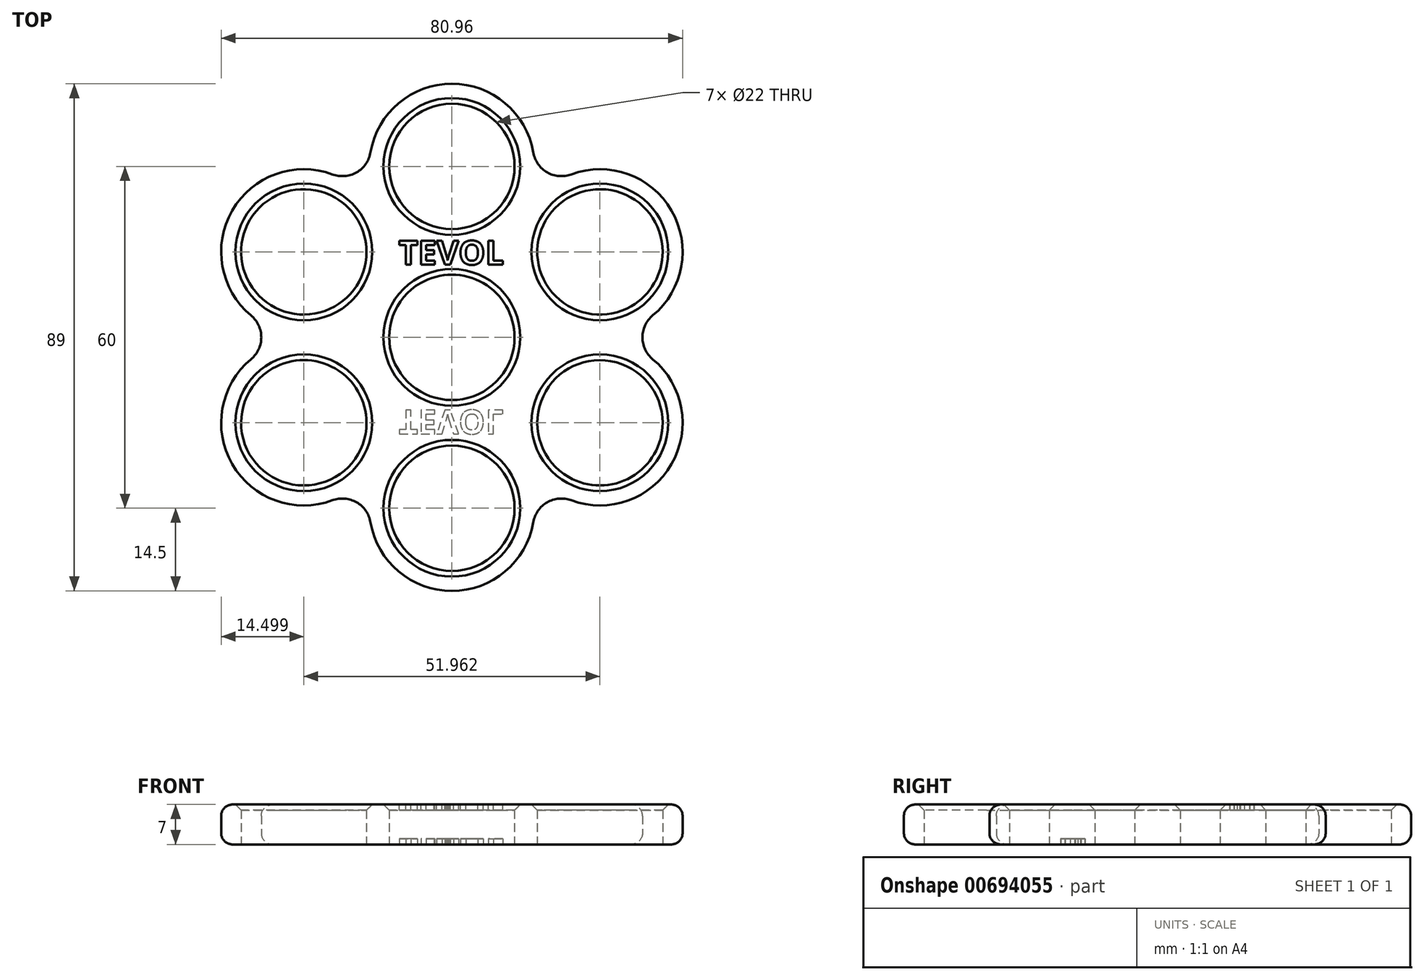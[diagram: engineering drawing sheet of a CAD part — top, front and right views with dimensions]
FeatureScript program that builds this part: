
annotation { "Feature Type Name" : "Feature", "Feature Type Description" : "" }
export const myFeature = defineFeature(function(context is Context, id is Id, definition is map)
    precondition{}
    {
        {
            var Q0;
            Q0=qCreatedBy(makeId("Top.planeOp"),FACE);
            var sketch = newSketch(context, id + "F0", { "sketchPlane" : qUnion([Q0])});
            skCircle(sketch, "E0", {"center": v(0, 0) * mm, "radius": 14.5 * mm});
            skCircle(sketch, "E1", {"center": v(0, -30) * mm, "radius": 14.5 * mm});
            skLineSegment(sketch, "E2", {"start": v(14.5, 0) * mm, "end": v(14.5, -30) * mm});
            skLineSegment(sketch, "E3", {"start": v(-14.5, 0) * mm, "end": v(-14.5, -30) * mm});
            skSolve(sketch);
        }
        {
            var Q0;
            Q0=qSketchRegion(id+"F0",true);
            var Q1;
            {var subQ0=sQuery(id+"F0.wireOp",EDGE,"E1");var subQ1=sQuery(id+"F0.wireOp",EDGE,"E0");var subQ2=makeQuery(id+"F0.imprint","INTERSECT",VERTEX,{"disambiguationData":[OD(0.0)],"derivedFrom":[subQ1,subQ0]});Q1=makeQuery(id+"F0.imprint","IMPRINT",FACE,{"disambiguationData":[TD([[makeQuery(id+"F0.imprint","IMPRINT",EDGE,{"disambiguationData":[TD([[subQ2,-1.0]])],"derivedFrom":subQ1}),1.0]])]});}
            extrude(context, id + "F1", {"entities" : qUnion([Q0, Q1]), "depth" : 7 * mm, "offsetDistance" : 25 * mm});
        }
        {
            var Q0;
            Q0=makeQuery(id+"F1.opExtrude","CAP_FACE",FACE,{"disambiguationData":[OSD([sQuery(id+"F0.wireOp",EDGE,"E0"),sQuery(id+"F0.wireOp",EDGE,"E1"),sQuery(id+"F0.wireOp",EDGE,"E2"),sQuery(id+"F0.wireOp",EDGE,"E3")])],"isStart":false});
            var sketch = newSketch(context, id + "F2", { "sketchPlane" : qUnion([Q0])});
            skCircle(sketch, "E4", {"center": v(0, 0) * mm, "radius": 11 * mm});
            skCircle(sketch, "E5", {"center": v(0, -30) * mm, "radius": 11 * mm});
            skLineSegment(sketch, "E6", {"start": v(0, 0) * mm, "end": v(0, -30) * mm});
            skSolve(sketch);
        }
        {
            var Q0;
            Q0=qSketchRegion(id+"F2",true);
            extrude(context, id + "F3", {"entities" : qUnion([Q0]), "operationType" : NewBodyOperationType.REMOVE, "endBound" : BoundingType.THROUGH_ALL, "oppositeDirection" : true, "depth" : 25 * mm, "offsetDistance" : 25 * mm});
        }
        {
            var Q0;
            Q0=qCreatedBy(makeId("Front.planeOp"),FACE);
            var sketch = newSketch(context, id + "F4", { "sketchPlane" : qUnion([Q0])});
            skLineSegment(sketch, "E7", {"start": v(0, 0) * mm, "end": v(0, 26.48) * mm});
            skSolve(sketch);
        }
        {
            var Q0;
            Q0=makeQuery(id+"F1.opExtrude","SWEPT_BODY",BODY,{"disambiguationData":[OSD([sQuery(id+"F0.wireOp",EDGE,"E0"),sQuery(id+"F0.wireOp",EDGE,"E1"),sQuery(id+"F0.wireOp",EDGE,"E2"),sQuery(id+"F0.wireOp",EDGE,"E3")])]});
            var Q1;
            Q1=sQuery(id+"F4.wireOp",EDGE,"E7");
            circularPattern(context, id + "F5", {"entities" : qUnion([Q0]), "axis" : qUnion([Q1]), "angle" : 360 * degree, "instanceCount" : 6, "equalSpace" : true});
        }
        {
            var Q0;
            Q0=makeQuery(id+"F5.opPattern","COPY",BODY,{"derivedFrom":makeQuery(id+"F1.opExtrude","SWEPT_BODY",BODY,{"disambiguationData":[OSD([sQuery(id+"F0.wireOp",EDGE,"E0"),sQuery(id+"F0.wireOp",EDGE,"E1"),sQuery(id+"F0.wireOp",EDGE,"E2"),sQuery(id+"F0.wireOp",EDGE,"E3")])]}),"instanceName":"4"});
            var Q1;
            Q1=makeQuery(id+"F5.opPattern","COPY",BODY,{"derivedFrom":makeQuery(id+"F1.opExtrude","SWEPT_BODY",BODY,{"disambiguationData":[OSD([sQuery(id+"F0.wireOp",EDGE,"E0"),sQuery(id+"F0.wireOp",EDGE,"E1"),sQuery(id+"F0.wireOp",EDGE,"E2"),sQuery(id+"F0.wireOp",EDGE,"E3")])]}),"instanceName":"3"});
            var Q2;
            Q2=makeQuery(id+"F5.opPattern","COPY",BODY,{"derivedFrom":makeQuery(id+"F1.opExtrude","SWEPT_BODY",BODY,{"disambiguationData":[OSD([sQuery(id+"F0.wireOp",EDGE,"E0"),sQuery(id+"F0.wireOp",EDGE,"E1"),sQuery(id+"F0.wireOp",EDGE,"E2"),sQuery(id+"F0.wireOp",EDGE,"E3")])]}),"instanceName":"2"});
            var Q3;
            Q3=makeQuery(id+"F5.opPattern","COPY",BODY,{"derivedFrom":makeQuery(id+"F1.opExtrude","SWEPT_BODY",BODY,{"disambiguationData":[OSD([sQuery(id+"F0.wireOp",EDGE,"E0"),sQuery(id+"F0.wireOp",EDGE,"E1"),sQuery(id+"F0.wireOp",EDGE,"E2"),sQuery(id+"F0.wireOp",EDGE,"E3")])]}),"instanceName":"1"});
            var Q4;
            Q4=makeQuery(id+"F1.opExtrude","SWEPT_BODY",BODY,{"disambiguationData":[OSD([sQuery(id+"F0.wireOp",EDGE,"E0"),sQuery(id+"F0.wireOp",EDGE,"E1"),sQuery(id+"F0.wireOp",EDGE,"E2"),sQuery(id+"F0.wireOp",EDGE,"E3")])]});
            var Q5;
            Q5=makeQuery(id+"F5.opPattern","COPY",BODY,{"derivedFrom":makeQuery(id+"F1.opExtrude","SWEPT_BODY",BODY,{"disambiguationData":[OSD([sQuery(id+"F0.wireOp",EDGE,"E0"),sQuery(id+"F0.wireOp",EDGE,"E1"),sQuery(id+"F0.wireOp",EDGE,"E2"),sQuery(id+"F0.wireOp",EDGE,"E3")])]}),"instanceName":"5"});
            booleanBodies(context, id + "F6", {"operationType" : BooleanOperationType.UNION, "tools" : qUnion([Q0, Q1, Q2, Q3, Q4, Q5])});
        }
        {
            var Q0;
            Q0=makeQuery(id+"F6.opBoolean","INTERSECT",EDGE,{"derivedFrom":[makeQuery(id+"F5.opPattern","COPY",FACE,{"derivedFrom":makeQuery(id+"F1.opExtrude","SWEPT_FACE",FACE,{"disambiguationData":[OSD([sQuery(id+"F0.wireOp",EDGE,"E2")])]}),"instanceName":"4"}),makeQuery(id+"F5.opPattern","COPY",FACE,{"derivedFrom":makeQuery(id+"F1.opExtrude","SWEPT_FACE",FACE,{"disambiguationData":[OSD([sQuery(id+"F0.wireOp",EDGE,"E3")])]}),"instanceName":"5"})]});
            var Q1;
            Q1=makeQuery(id+"F6.opBoolean","INTERSECT",EDGE,{"derivedFrom":[makeQuery(id+"F1.opExtrude","SWEPT_FACE",FACE,{"disambiguationData":[OSD([sQuery(id+"F0.wireOp",EDGE,"E3")])]}),makeQuery(id+"F5.opPattern","COPY",FACE,{"derivedFrom":makeQuery(id+"F1.opExtrude","SWEPT_FACE",FACE,{"disambiguationData":[OSD([sQuery(id+"F0.wireOp",EDGE,"E2")])]}),"instanceName":"5"})]});
            var Q2;
            Q2=makeQuery(id+"F6.opBoolean","INTERSECT",EDGE,{"derivedFrom":[makeQuery(id+"F1.opExtrude","SWEPT_FACE",FACE,{"disambiguationData":[OSD([sQuery(id+"F0.wireOp",EDGE,"E2")])]}),makeQuery(id+"F5.opPattern","COPY",FACE,{"derivedFrom":makeQuery(id+"F1.opExtrude","SWEPT_FACE",FACE,{"disambiguationData":[OSD([sQuery(id+"F0.wireOp",EDGE,"E3")])]}),"instanceName":"1"})]});
            var Q3;
            Q3=makeQuery(id+"F6.opBoolean","INTERSECT",EDGE,{"derivedFrom":[makeQuery(id+"F5.opPattern","COPY",FACE,{"derivedFrom":makeQuery(id+"F1.opExtrude","SWEPT_FACE",FACE,{"disambiguationData":[OSD([sQuery(id+"F0.wireOp",EDGE,"E2")])]}),"instanceName":"1"}),makeQuery(id+"F5.opPattern","COPY",FACE,{"derivedFrom":makeQuery(id+"F1.opExtrude","SWEPT_FACE",FACE,{"disambiguationData":[OSD([sQuery(id+"F0.wireOp",EDGE,"E3")])]}),"instanceName":"2"})]});
            var Q4;
            {var subQ0=makeQuery(id+"F1.opExtrude","SWEPT_FACE",FACE,{"disambiguationData":[OSD([sQuery(id+"F0.wireOp",EDGE,"E3")])]});Q4=makeQuery(id+"F6.opBoolean","INTERSECT",EDGE,{"derivedFrom":[makeQuery(id+"F5.opPattern","COPY",FACE,{"derivedFrom":subQ0,"instanceName":"3"}),makeQuery(id+"F5.opPattern","COPY",FACE,{"derivedFrom":subQ0,"instanceName":"5"})]});}
            var Q5;
            Q5=makeQuery(id+"F6.opBoolean","INTERSECT",EDGE,{"derivedFrom":[makeQuery(id+"F5.opPattern","COPY",FACE,{"derivedFrom":makeQuery(id+"F1.opExtrude","SWEPT_FACE",FACE,{"disambiguationData":[OSD([sQuery(id+"F0.wireOp",EDGE,"E2")])]}),"instanceName":"3"}),makeQuery(id+"F5.opPattern","COPY",FACE,{"derivedFrom":makeQuery(id+"F1.opExtrude","SWEPT_FACE",FACE,{"disambiguationData":[OSD([sQuery(id+"F0.wireOp",EDGE,"E3")])]}),"instanceName":"4"})]});
            fillet(context, id + "F7", {"entities" : qUnion([Q0, Q1, Q2, Q3, Q4, Q5]), "radius" : 5 * mm, "tangentPropagation" : true, "allowEdgeOverflow" : false});
        }
        {
            var Q0;
            Q0=makeQuery(id+"F5.opPattern","COPY",EDGE,{"derivedFrom":makeQuery(id+"F1.opExtrude","CAP_EDGE",EDGE,{"disambiguationData":[OSD([sQuery(id+"F0.wireOp",EDGE,"E1")])],"isStart":false}),"instanceName":"1"});
            var Q1;
            Q1=makeQuery(id+"F1.opExtrude","CAP_EDGE",EDGE,{"disambiguationData":[OSD([sQuery(id+"F0.wireOp",EDGE,"E1")])],"isStart":true});
            fillet(context, id + "F8", {"entities" : qUnion([Q0, Q1]), "radius" : 2 * mm, "tangentPropagation" : true, "allowEdgeOverflow" : false});
        }
        {
            var Q0;
            Q0=makeQuery(id+"F5.opPattern","COPY",EDGE,{"derivedFrom":makeQuery(id+"F3.boolean.opBoolean","COPY",EDGE,{"derivedFrom":makeQuery(id+"F3.opExtrude","CAP_EDGE",EDGE,{"disambiguationData":[OSD([sQuery(id+"F2.wireOp",EDGE,"E4")])],"isStart":true})}),"instanceName":"4"});
            var Q1;
            Q1=makeQuery(id+"F5.opPattern","COPY",EDGE,{"derivedFrom":makeQuery(id+"F3.boolean.opBoolean","COPY",EDGE,{"derivedFrom":makeQuery(id+"F3.opExtrude","CAP_EDGE",EDGE,{"disambiguationData":[OSD([sQuery(id+"F2.wireOp",EDGE,"E5")])],"isStart":true})}),"instanceName":"2"});
            var Q2;
            Q2=makeQuery(id+"F5.opPattern","COPY",EDGE,{"derivedFrom":makeQuery(id+"F3.boolean.opBoolean","COPY",EDGE,{"derivedFrom":makeQuery(id+"F3.opExtrude","CAP_EDGE",EDGE,{"disambiguationData":[OSD([sQuery(id+"F2.wireOp",EDGE,"E5")])],"isStart":true})}),"instanceName":"3"});
            var Q3;
            Q3=makeQuery(id+"F5.opPattern","COPY",EDGE,{"derivedFrom":makeQuery(id+"F3.boolean.opBoolean","COPY",EDGE,{"derivedFrom":makeQuery(id+"F3.opExtrude","CAP_EDGE",EDGE,{"disambiguationData":[OSD([sQuery(id+"F2.wireOp",EDGE,"E5")])],"isStart":true})}),"instanceName":"4"});
            var Q4;
            Q4=makeQuery(id+"F5.opPattern","COPY",EDGE,{"derivedFrom":makeQuery(id+"F3.boolean.opBoolean","COPY",EDGE,{"derivedFrom":makeQuery(id+"F3.opExtrude","CAP_EDGE",EDGE,{"disambiguationData":[OSD([sQuery(id+"F2.wireOp",EDGE,"E5")])],"isStart":true})}),"instanceName":"5"});
            var Q5;
            Q5=makeQuery(id+"F3.boolean.opBoolean","COPY",EDGE,{"derivedFrom":makeQuery(id+"F3.opExtrude","CAP_EDGE",EDGE,{"disambiguationData":[OSD([sQuery(id+"F2.wireOp",EDGE,"E5")])],"isStart":true})});
            var Q6;
            Q6=makeQuery(id+"F5.opPattern","COPY",EDGE,{"derivedFrom":makeQuery(id+"F3.boolean.opBoolean","COPY",EDGE,{"derivedFrom":makeQuery(id+"F3.opExtrude","CAP_EDGE",EDGE,{"disambiguationData":[OSD([sQuery(id+"F2.wireOp",EDGE,"E5")])],"isStart":true})}),"instanceName":"1"});
            var Q7;
            Q7=makeQuery(id+"F5.opPattern","COPY",EDGE,{"derivedFrom":makeQuery(id+"F3.boolean.opBoolean","INTERSECT",EDGE,{"derivedFrom":[makeQuery(id+"F1.opExtrude","CAP_FACE",FACE,{"disambiguationData":[OSD([sQuery(id+"F0.wireOp",EDGE,"E0"),sQuery(id+"F0.wireOp",EDGE,"E1"),sQuery(id+"F0.wireOp",EDGE,"E2"),sQuery(id+"F0.wireOp",EDGE,"E3")])],"isStart":true}),makeQuery(id+"F3.opExtrude","SWEPT_FACE",FACE,{"disambiguationData":[OSD([sQuery(id+"F2.wireOp",EDGE,"E5")])]})]}),"instanceName":"5"});
            var Q8;
            Q8=makeQuery(id+"F3.boolean.opBoolean","INTERSECT",EDGE,{"derivedFrom":[makeQuery(id+"F1.opExtrude","CAP_FACE",FACE,{"disambiguationData":[OSD([sQuery(id+"F0.wireOp",EDGE,"E0"),sQuery(id+"F0.wireOp",EDGE,"E1"),sQuery(id+"F0.wireOp",EDGE,"E2"),sQuery(id+"F0.wireOp",EDGE,"E3")])],"isStart":true}),makeQuery(id+"F3.opExtrude","SWEPT_FACE",FACE,{"disambiguationData":[OSD([sQuery(id+"F2.wireOp",EDGE,"E5")])]})]});
            var Q9;
            Q9=makeQuery(id+"F5.opPattern","COPY",EDGE,{"derivedFrom":makeQuery(id+"F3.boolean.opBoolean","INTERSECT",EDGE,{"derivedFrom":[makeQuery(id+"F1.opExtrude","CAP_FACE",FACE,{"disambiguationData":[OSD([sQuery(id+"F0.wireOp",EDGE,"E0"),sQuery(id+"F0.wireOp",EDGE,"E1"),sQuery(id+"F0.wireOp",EDGE,"E2"),sQuery(id+"F0.wireOp",EDGE,"E3")])],"isStart":true}),makeQuery(id+"F3.opExtrude","SWEPT_FACE",FACE,{"disambiguationData":[OSD([sQuery(id+"F2.wireOp",EDGE,"E5")])]})]}),"instanceName":"1"});
            var Q10;
            Q10=makeQuery(id+"F5.opPattern","COPY",EDGE,{"derivedFrom":makeQuery(id+"F3.boolean.opBoolean","INTERSECT",EDGE,{"derivedFrom":[makeQuery(id+"F1.opExtrude","CAP_FACE",FACE,{"disambiguationData":[OSD([sQuery(id+"F0.wireOp",EDGE,"E0"),sQuery(id+"F0.wireOp",EDGE,"E1"),sQuery(id+"F0.wireOp",EDGE,"E2"),sQuery(id+"F0.wireOp",EDGE,"E3")])],"isStart":true}),makeQuery(id+"F3.opExtrude","SWEPT_FACE",FACE,{"disambiguationData":[OSD([sQuery(id+"F2.wireOp",EDGE,"E5")])]})]}),"instanceName":"2"});
            var Q11;
            Q11=makeQuery(id+"F5.opPattern","COPY",EDGE,{"derivedFrom":makeQuery(id+"F3.boolean.opBoolean","INTERSECT",EDGE,{"derivedFrom":[makeQuery(id+"F1.opExtrude","CAP_FACE",FACE,{"disambiguationData":[OSD([sQuery(id+"F0.wireOp",EDGE,"E0"),sQuery(id+"F0.wireOp",EDGE,"E1"),sQuery(id+"F0.wireOp",EDGE,"E2"),sQuery(id+"F0.wireOp",EDGE,"E3")])],"isStart":true}),makeQuery(id+"F3.opExtrude","SWEPT_FACE",FACE,{"disambiguationData":[OSD([sQuery(id+"F2.wireOp",EDGE,"E5")])]})]}),"instanceName":"3"});
            var Q12;
            Q12=makeQuery(id+"F5.opPattern","COPY",EDGE,{"derivedFrom":makeQuery(id+"F3.boolean.opBoolean","INTERSECT",EDGE,{"derivedFrom":[makeQuery(id+"F1.opExtrude","CAP_FACE",FACE,{"disambiguationData":[OSD([sQuery(id+"F0.wireOp",EDGE,"E0"),sQuery(id+"F0.wireOp",EDGE,"E1"),sQuery(id+"F0.wireOp",EDGE,"E2"),sQuery(id+"F0.wireOp",EDGE,"E3")])],"isStart":true}),makeQuery(id+"F3.opExtrude","SWEPT_FACE",FACE,{"disambiguationData":[OSD([sQuery(id+"F2.wireOp",EDGE,"E4")])]})]}),"instanceName":"4"});
            var Q13;
            Q13=makeQuery(id+"F5.opPattern","COPY",EDGE,{"derivedFrom":makeQuery(id+"F3.boolean.opBoolean","INTERSECT",EDGE,{"derivedFrom":[makeQuery(id+"F1.opExtrude","CAP_FACE",FACE,{"disambiguationData":[OSD([sQuery(id+"F0.wireOp",EDGE,"E0"),sQuery(id+"F0.wireOp",EDGE,"E1"),sQuery(id+"F0.wireOp",EDGE,"E2"),sQuery(id+"F0.wireOp",EDGE,"E3")])],"isStart":true}),makeQuery(id+"F3.opExtrude","SWEPT_FACE",FACE,{"disambiguationData":[OSD([sQuery(id+"F2.wireOp",EDGE,"E5")])]})]}),"instanceName":"4"});
            chamfer(context, id + "F9", {"entities" : qUnion([Q0, Q1, Q2, Q3, Q4, Q5, Q6, Q7, Q8, Q9, Q10, Q11, Q12, Q13]), "width" : 1 * mm, "tangentPropagation" : true});
        }
        {
            var Q0;
            Q0=qCreatedBy(makeId("Top.planeOp"),FACE);
            cPlane(context, id + "F10", {"entities" : qUnion([Q0]), "cplaneType" : CPlaneType.OFFSET, "offset" : 7 * mm, "width" : 150 * mm, "height" : 150 * mm});
        }
        {
            var Q0;
            Q0=qCreatedBy(id+"F10.planeOp",FACE);
            var sketch = newSketch(context, id + "F11", { "sketchPlane" : qUnion([Q0])});
            skText(sketch, "E8", { "text": "TEVOL", "fontName": "NotoSans-Bold.ttf"});
            const initialGuessF11  = {"E8": [-0.00934, 0.01275, 1, 0, 0.00423]};
            skSetInitialGuess(sketch, initialGuessF11);
            skSolve(sketch);
        }
        {
            var Q0;
            Q0 = qSketchRegion(id + "F11", true);
            extrude(context, id + "F12", {"entities" : qUnion([Q0]), "operationType" : NewBodyOperationType.REMOVE, "oppositeDirection" : true, "depth" : 1 * mm, "offsetDistance" : 25 * mm});
        }
        {
            var Q0;
            Q0=makeQuery(id+"F5.opPattern","COPY",BODY,{"derivedFrom":makeQuery(id+"F1.opExtrude","SWEPT_BODY",BODY,{"disambiguationData":[OSD([sQuery(id+"F0.wireOp",EDGE,"E0"),sQuery(id+"F0.wireOp",EDGE,"E1"),sQuery(id+"F0.wireOp",EDGE,"E2"),sQuery(id+"F0.wireOp",EDGE,"E3")])]}),"instanceName":"4"});
            var Q1;
            Q1=sQuery(id+"F4.wireOp",EDGE,"E7");
            transform(context, id + "F13", {"entities" : qUnion([Q0]), "transformType" : TransformType.ROTATION, "transformAxis" : qUnion([Q1]), "angle" : 180 * degree, "makeCopy" : false});
        }
        {
            var Q0;
            Q0=makeQuery(id+"F5.opPattern","COPY",BODY,{"derivedFrom":makeQuery(id+"F1.opExtrude","SWEPT_BODY",BODY,{"disambiguationData":[OSD([sQuery(id+"F0.wireOp",EDGE,"E0"),sQuery(id+"F0.wireOp",EDGE,"E1"),sQuery(id+"F0.wireOp",EDGE,"E2"),sQuery(id+"F0.wireOp",EDGE,"E3")])]}),"instanceName":"4"});
            var Q1;
            Q1=sQuery(id+"F2.wireOp",EDGE,"E6");
            var Q2;
            Q2=sQuery(id+"F2.wireOp",EDGE,"E6");
            transform(context, id + "F14", {"entities" : qUnion([Q0]), "transformType" : TransformType.ROTATION, "transformAxis" : qUnion([Q2]), "angle" : 180 * degree, "makeCopy" : false});
        }
        {
            var Q0;
            Q0=makeQuery(id+"F5.opPattern","COPY",BODY,{"derivedFrom":makeQuery(id+"F1.opExtrude","SWEPT_BODY",BODY,{"disambiguationData":[OSD([sQuery(id+"F0.wireOp",EDGE,"E0"),sQuery(id+"F0.wireOp",EDGE,"E1"),sQuery(id+"F0.wireOp",EDGE,"E2"),sQuery(id+"F0.wireOp",EDGE,"E3")])]}),"instanceName":"4"});
            var Q1;
            Q1=sQuery(id+"F4.wireOp",EDGE,"E7");
            var Q2;
            Q2=sQuery(id+"F4.wireOp",EDGE,"E7");
            transform(context, id + "F15", {"entities" : qUnion([Q0]), "transformType" : TransformType.TRANSLATION_DISTANCE, "transformDirection" : qUnion([Q2]), "distance" : 7 * mm, "oppositeDirection" : true, "makeCopy" : false});
        }
        {
            var Q0;
            Q0 = qSketchRegion(id + "F11", true);
            extrude(context, id + "F16", {"entities" : qUnion([Q0]), "operationType" : NewBodyOperationType.REMOVE, "oppositeDirection" : true, "depth" : 1 * mm, "offsetDistance" : 25 * mm});
        }
    });
